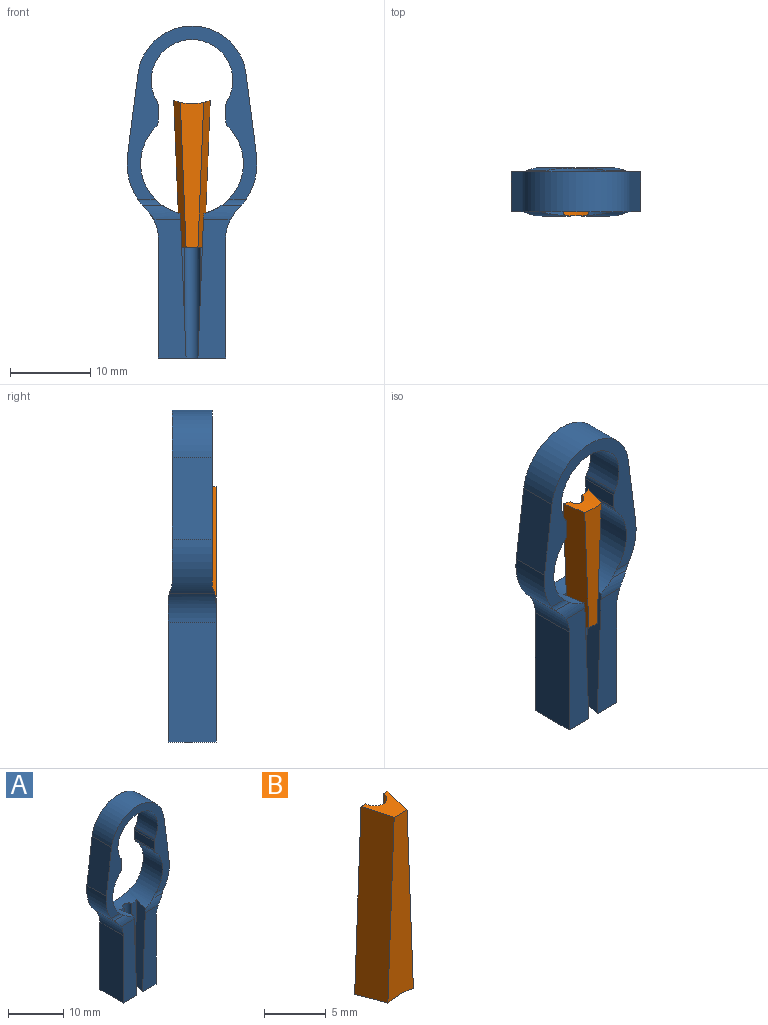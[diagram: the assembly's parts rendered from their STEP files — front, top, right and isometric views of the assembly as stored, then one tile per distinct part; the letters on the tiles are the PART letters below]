
ASSEMBLY  parts=2 mates=1
PART A: 35 faces, bbox 16.3x6x41.5 mm
  f0: cylinder r=6.42mm len=12.85mm, axis (0,1,0), area 145.3mm2, adj f11,f12,f21,f22,f23,f24,f25,f26
  f1: plane 10.21x5mm, normal (-0.99,0,0.13), area 51.5mm2, adj f2,f8,f26,f31
  f2: cylinder r=8.12mm len=6.83mm, axis (0,1,0), area 38mm2, adj f1,f19,f26,f28,f30,f31,f33,f34
  f3: cylinder r=8.12mm len=6.83mm, axis (0,1,0), area 38mm2, adj f4,f20,f26,f27,f29,f31,f32,f33
  f4: plane 10.21x5mm, normal (0.99,0,0.13), area 51.5mm2, adj f3,f8,f26,f31
  f5: cylinder r=5.1mm len=10.2mm, axis (0,1,0), area 108.2mm2, adj f10,f13,f26,f31
  f6: plane 5x1.89mm, normal (-1,0,0), area 9.4mm2, adj f10,f11,f26,f31
  f7: plane 5x1.89mm, normal (1,0,0), area 9.4mm2, adj f12,f13,f26,f31
  f8: cylinder r=6.8mm len=13.49mm, axis (0,1,0), area 98.1mm2, adj f1,f4,f26,f31
  f9: plane 17.25x4.02mm, normal (0,-1,0), area 54.2mm2, adj f14,f15,f19,f24,f34
  f10: cylinder r=1mm len=5mm, axis (0,1,0), area 2.8mm2, adj f5,f6,f26,f31
  f11: cylinder r=1mm len=5mm, axis (0,1,0), area 4mm2, adj f0,f6,f26,f31
  f12: cylinder r=1mm len=5mm, axis (0,1,0), area 4mm2, adj f0,f7,f26,f31
  f13: cylinder r=1mm len=5mm, axis (0,1,0), area 2.8mm2, adj f5,f7,f26,f31
  f14: plane 14.96x6mm, normal (-1,0,0), area 89.8mm2, adj f9,f15,f18,f19
  f15: plane 8.4x6mm, normal (0,0,-1), area 42mm2, adj f9,f14,f16,f17,f18,f21,f22,f23
  f16: plane 14.96x6mm, normal (1,0,0), area 89.8mm2, adj f15,f17,f18,f20
  f17: plane 17.25x4.02mm, normal (0,-1,0), area 54.2mm2, adj f15,f16,f20,f23,f32
  f18: plane 17.25x9.51mm, normal (0,1,0), area 145.8mm2, adj f14,f15,f16,f19,f20,f33
  f19: cylinder r=5mm len=6mm, axis (0,1,0), area 23.6mm2, adj f2,f9,f14,f18,f33,f34
  f20: cylinder r=5mm len=6mm, axis (0,1,0), area 23.6mm2, adj f3,f16,f17,f18,f32,f33
  f21: cylinder r=1mm len=17.98mm, axis (0,0,-1), area 56.4mm2, adj f0,f15,f22,f25
  f22: plane 18.32x1.28mm, normal (0,-1,0), area 16.4mm2, adj f0,f15,f21,f23
  f23: plane 18.35x3.03mm, normal (-0.97,0.26,0.04), area 56.5mm2, adj f0,f15,f17,f22,f32
  f24: plane 18.35x3.03mm, normal (0.97,0.26,0.04), area 56.5mm2, adj f0,f9,f15,f25,f34
  f25: plane 18.32x1.28mm, normal (0,-1,0), area 16.4mm2, adj f0,f15,f21,f24
  f26: plane 21.65x16.25mm, normal (0,-1,0), area 98.5mm2, adj f0,f1,f2,f3,f4,f5,f6,f7
  f27: cylinder r=2mm len=3.03mm, axis (1,0,0), area 1.8mm2, adj f0,f3,f26,f32
  f28: cylinder r=2mm len=3.03mm, axis (1,0,0), area 1.8mm2, adj f0,f2,f26,f34
  f29: cylinder r=2mm len=3.03mm, axis (1,0,0), area 1.8mm2, adj f0,f3,f31,f33
  f30: cylinder r=2mm len=3.03mm, axis (1,0,0), area 1.8mm2, adj f0,f2,f31,f33
  f31: plane 21.65x16.25mm, normal (0,1,0), area 98.5mm2, adj f0,f1,f2,f3,f4,f5,f6,f7
  f32: cylinder r=5mm len=4.8mm, axis (1,0,0), area 6.1mm2, adj f0,f3,f17,f20,f23,f27
  f33: cylinder r=5mm len=12.46mm, axis (1,0,0), area 14.3mm2, adj f0,f2,f3,f18,f19,f20,f29,f30
  f34: cylinder r=5mm len=4.8mm, axis (1,0,0), area 6.1mm2, adj f0,f2,f9,f19,f24,f28
PART B: 8 faces, bbox 4.6x3x18.3 mm
  f0: plane 3.09x3mm, normal (0,0,1), area 5.3mm2, adj f2,f3,f4,f5,f6,f7
  f1: cylinder r=6.42mm len=4.55mm, axis (0,1,0), area 9.8mm2, adj f2,f3,f4,f5,f6,f7
  f2: plane 18.07x2.93mm, normal (0,-1,0), area 39.5mm2, adj f0,f1,f6,f7
  f3: plane 18.32x1.28mm, normal (0,1,0), area 16.4mm2, adj f0,f1,f5,f6
  f4: plane 18.32x1.28mm, normal (0,1,0), area 16.4mm2, adj f0,f1,f5,f7
  f5: cylinder r=1mm len=17.98mm, axis (0,0,-1), area 56.4mm2, adj f0,f1,f3,f4
  f6: plane 18.32x3mm, normal (0.97,-0.26,0.04), area 56.5mm2, adj f0,f1,f2,f3
  f7: plane 18.32x3mm, normal (-0.97,-0.26,0.04), area 56.5mm2, adj f0,f1,f2,f4
PLACE A t=(4.2,0,31.81)mm
PLACE B rot(axis=(0,1,0),180deg) t=(6.5,-3,32.86)mm
MATE slider A.f21 <-> B.f5  axis (0,0,-1) through (4.2,-3,0)mm
